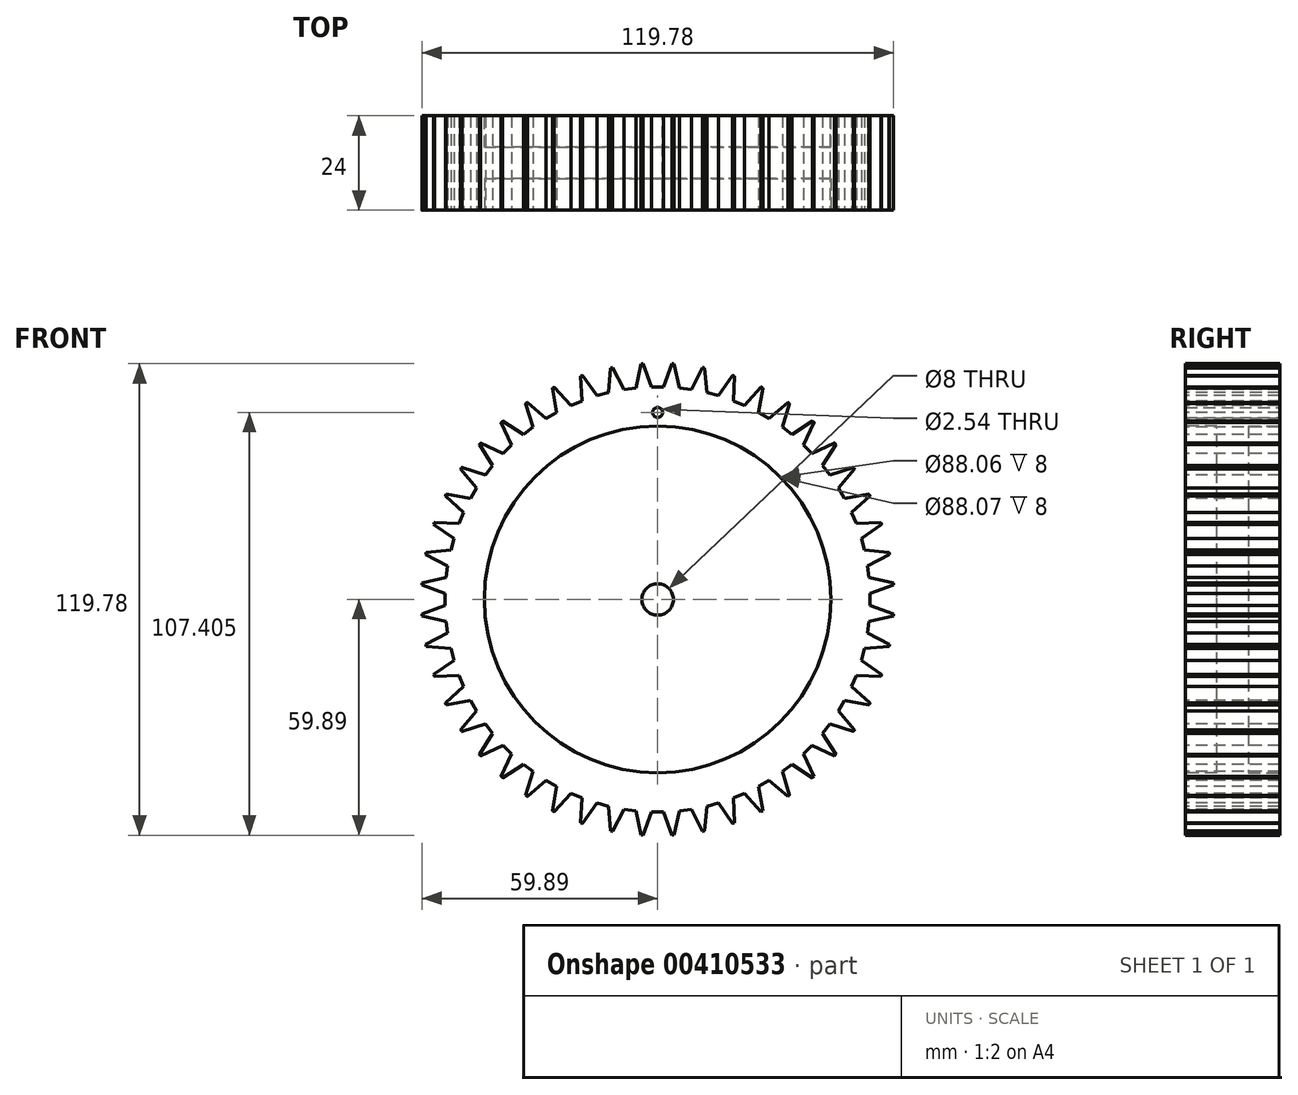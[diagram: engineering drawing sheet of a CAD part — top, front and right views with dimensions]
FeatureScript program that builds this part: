
annotation { "Feature Type Name" : "Feature", "Feature Type Description" : "" }
export const myFeature = defineFeature(function(context is Context, id is Id, definition is map)
    precondition{}
    {
        {
            var Q0;
            Q0=qCreatedBy(makeId("Front.planeOp"),FACE);
            var sketch = newSketch(context, id + "F0", { "sketchPlane" : qUnion([Q0])});
            skCircle(sketch, "E0", {"center": v(0, 0) * mm, "radius": 60 * mm});
            skCircle(sketch, "E1", {"center": v(0, 0) * mm, "radius": 55 * mm, "construction": true});
            skLineSegment(sketch, "E2", {"start": v(0, 74.4) * mm, "end": v(0, -8.78) * mm, "construction": true});
            skCircle(sketch, "E3", {"center": v(0, 0) * mm, "radius": 4 * mm});
            skCircle(sketch, "E4", {"center": v(0, 47.51) * mm, "radius": 1.27 * mm});
            skSolve(sketch);
        }
        {
            var Q0;
            Q0=makeQuery(id+"F0.imprint","IMPRINT",FACE,{"disambiguationData":[TD([[makeQuery(id+"F0.imprint","IMPRINT",EDGE,{"derivedFrom":sQuery(id+"F0.wireOp",EDGE,"E0")}),1.0]])]});
            extrude(context, id + "F1", {"entities" : qUnion([Q0]), "depth" : 24 * mm, "symmetric" : true});
        }
        {
            var Q0;
            Q0=qCreatedBy(makeId("Front.planeOp"),FACE);
            var sketch = newSketch(context, id + "F2", { "sketchPlane" : qUnion([Q0])});
            skLineSegment(sketch, "E5", {"start": v(1.52, 53.99) * mm, "end": v(3.7, 59.99) * mm});
            skLineSegment(sketch, "E6.MirrorCS", {"start": v(-1.52, 53.99) * mm, "end": v(-3.7, 59.99) * mm});
            skLineSegment(sketch, "E7", {"start": v(-1.52, 53.99) * mm, "end": v(1.52, 53.99) * mm});
            skCircle(sketch, "E8.0", {"center": v(0, 0) * mm, "radius": 60 * mm});
            skArc(sketch, "E9", {"start": v(3.7, 59.99) * mm, "mid": v(0, 60.13) * mm, "end": v(-3.7, 59.99) * mm});
            skSolve(sketch);
        }
        {
            var Q0;
            Q0=makeQuery(id+"F2.imprint","IMPRINT",FACE,{"disambiguationData":[TD([[makeQuery(id+"F2.imprint","IMPRINT",EDGE,{"derivedFrom":sQuery(id+"F2.wireOp",EDGE,"E5")}),1.0]])]});
            extrude(context, id + "F3", {"entities" : qUnion([Q0]), "operationType" : NewBodyOperationType.REMOVE, "oppositeDirection" : true, "depth" : 24 * mm, "symmetric" : true});
        }
        {
            var Q0;
            Q0=makeQuery(id+"F3.boolean.opBoolean","COPY",FACE,{"derivedFrom":makeQuery(id+"F3.opExtrude","SWEPT_FACE",FACE,{"disambiguationData":[OSD([sQuery(id+"F2.wireOp",EDGE,"E7")])]})});
            var Q1;
            Q1=makeQuery(id+"F3.boolean.opBoolean","COPY",FACE,{"derivedFrom":makeQuery(id+"F3.opExtrude","SWEPT_FACE",FACE,{"disambiguationData":[OSD([sQuery(id+"F2.wireOp",EDGE,"E6.MirrorCS")])]})});
            var Q2;
            Q2=makeQuery(id+"F3.boolean.opBoolean","COPY",FACE,{"derivedFrom":makeQuery(id+"F3.opExtrude","SWEPT_FACE",FACE,{"disambiguationData":[OSD([sQuery(id+"F2.wireOp",EDGE,"E5")])]})});
            var Q3;
            Q3=sQuery(id+"F0.wireOp",EDGE,"E1");
            circularPattern(context, id + "F4", {"patternType" : PatternType.FACE, "faces" : qUnion([Q0, Q1, Q2]), "axis" : qUnion([Q3]), "angle" : 360 * degree, "instanceCount" : 48, "equalSpace" : true, "computeTransformsWithoutBuiltin" : true});
        }
        {
            var Q0;
            Q0=makeQuery(id+"F1.opExtrude","CAP_FACE",FACE,{"disambiguationData":[OSD([sQuery(id+"F0.wireOp",EDGE,"E0"),sQuery(id+"F0.wireOp",EDGE,"E3"),sQuery(id+"F0.wireOp",EDGE,"E4")])],"isStart":false});
            var sketch = newSketch(context, id + "F5", { "sketchPlane" : qUnion([Q0])});
            skCircle(sketch, "E10", {"center": v(0, 0) * mm, "radius": 44.03 * mm});
            skSolve(sketch);
        }
        {
            var Q0;
            Q0=makeQuery(id+"F5.imprint","IMPRINT",FACE,{"disambiguationData":[TD([[makeQuery(id+"F5.imprint","IMPRINT",EDGE,{"derivedFrom":sQuery(id+"F5.wireOp",EDGE,"E10")}),1.0]])]});
            extrude(context, id + "F6", {"entities" : qUnion([Q0]), "operationType" : NewBodyOperationType.REMOVE, "oppositeDirection" : true, "depth" : 8 * mm});
        }
        {
            var Q0;
            Q0=makeQuery(id+"F1.opExtrude","CAP_FACE",FACE,{"disambiguationData":[OSD([sQuery(id+"F0.wireOp",EDGE,"E0"),sQuery(id+"F0.wireOp",EDGE,"E3"),sQuery(id+"F0.wireOp",EDGE,"E4")])],"isStart":true});
            var sketch = newSketch(context, id + "F7", { "sketchPlane" : qUnion([Q0])});
            skCircle(sketch, "E11.0", {"center": v(0, 0) * mm, "radius": 44.03 * mm});
            skCircle(sketch, "E12", {"center": v(0, 0) * mm, "radius": 44.04 * mm});
            skCircle(sketch, "E13", {"center": v(0, 0) * mm, "radius": 10.95 * mm});
            skSolve(sketch);
        }
        {
            var Q0;
            Q0=makeQuery(id+"F7.imprint","IMPRINT",FACE,{"disambiguationData":[TD([[makeQuery(id+"F7.imprint","IMPRINT",EDGE,{"derivedFrom":sQuery(id+"F7.wireOp",EDGE,"E11.0")}),-1.0]])]});
            extrude(context, id + "F8", {"entities" : qUnion([Q0]), "operationType" : NewBodyOperationType.REMOVE, "oppositeDirection" : true, "depth" : 8 * mm});
        }
    });
